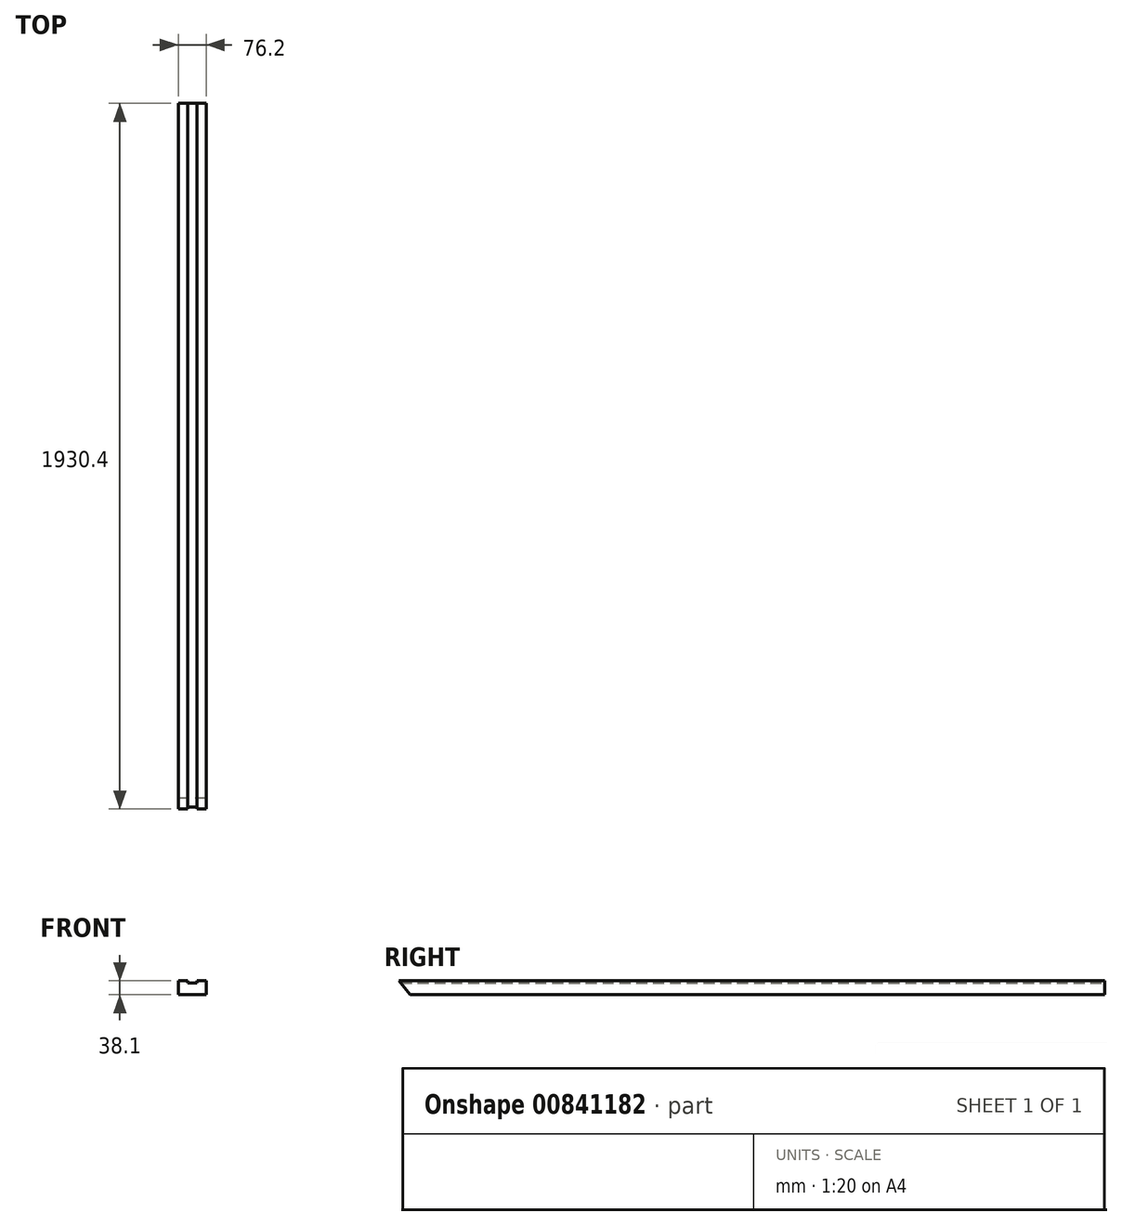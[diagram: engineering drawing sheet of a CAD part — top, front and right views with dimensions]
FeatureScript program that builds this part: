
annotation { "Feature Type Name" : "Feature", "Feature Type Description" : "" }
export const myFeature = defineFeature(function(context is Context, id is Id, definition is map)
    precondition{}
    {
        {
            var Q0;
            Q0=qCreatedBy(makeId("Front.planeOp"),FACE);
            var sketch = newSketch(context, id + "F0", { "sketchPlane" : qUnion([Q0])});
            skLineSegment(sketch, "E0.bottom", {"start": v(0, 0) * mm, "end": v(76.2, 0) * mm});
            skLineSegment(sketch, "E0.top", {"start": v(0, 38.1) * mm, "end": v(25.4, 38.1) * mm});
            skLineSegment(sketch, "E0.left", {"start": v(0, 0) * mm, "end": v(0, 38.1) * mm});
            skLineSegment(sketch, "E0.right", {"start": v(76.2, 0) * mm, "end": v(76.2, 38.1) * mm});
            skLineSegment(sketch, "E1", {"start": v(25.4, 38.1) * mm, "end": v(25.4, 31.75) * mm});
            skLineSegment(sketch, "E2", {"start": v(25.4, 31.75) * mm, "end": v(50.8, 31.75) * mm});
            skLineSegment(sketch, "E3", {"start": v(50.8, 31.75) * mm, "end": v(50.8, 38.1) * mm});
            skLineSegment(sketch, "E4.trimOffspring", {"start": v(50.8, 38.1) * mm, "end": v(76.2, 38.1) * mm});
            skSolve(sketch);
        }
        {
            var Q0;
            Q0=makeQuery(id+"F0.imprint","IMPRINT",FACE,{"disambiguationData":[TD([[makeQuery(id+"F0.imprint","IMPRINT",EDGE,{"derivedFrom":sQuery(id+"F0.wireOp",EDGE,"E0.bottom")}),1.0]])]});
            extrude(context, id + "F1", {"entities" : qUnion([Q0]), "depth" : 1930.4 * mm, "offsetDistance" : 25.4 * mm});
        }
        {
            var Q0;
            Q0=makeQuery(id+"F1.opExtrude","CAP_EDGE",EDGE,{"disambiguationData":[OSD([sQuery(id+"F0.wireOp",EDGE,"E0.bottom")])],"isStart":false});
            chamfer(context, id + "F2", {"entities" : qUnion([Q0]), "chamferType" : ChamferType.OFFSET_ANGLE, "width" : 38.1 * mm, "oppositeDirection" : false, "angle" : 38 * degree, "tangentPropagation" : true});
        }
    });
